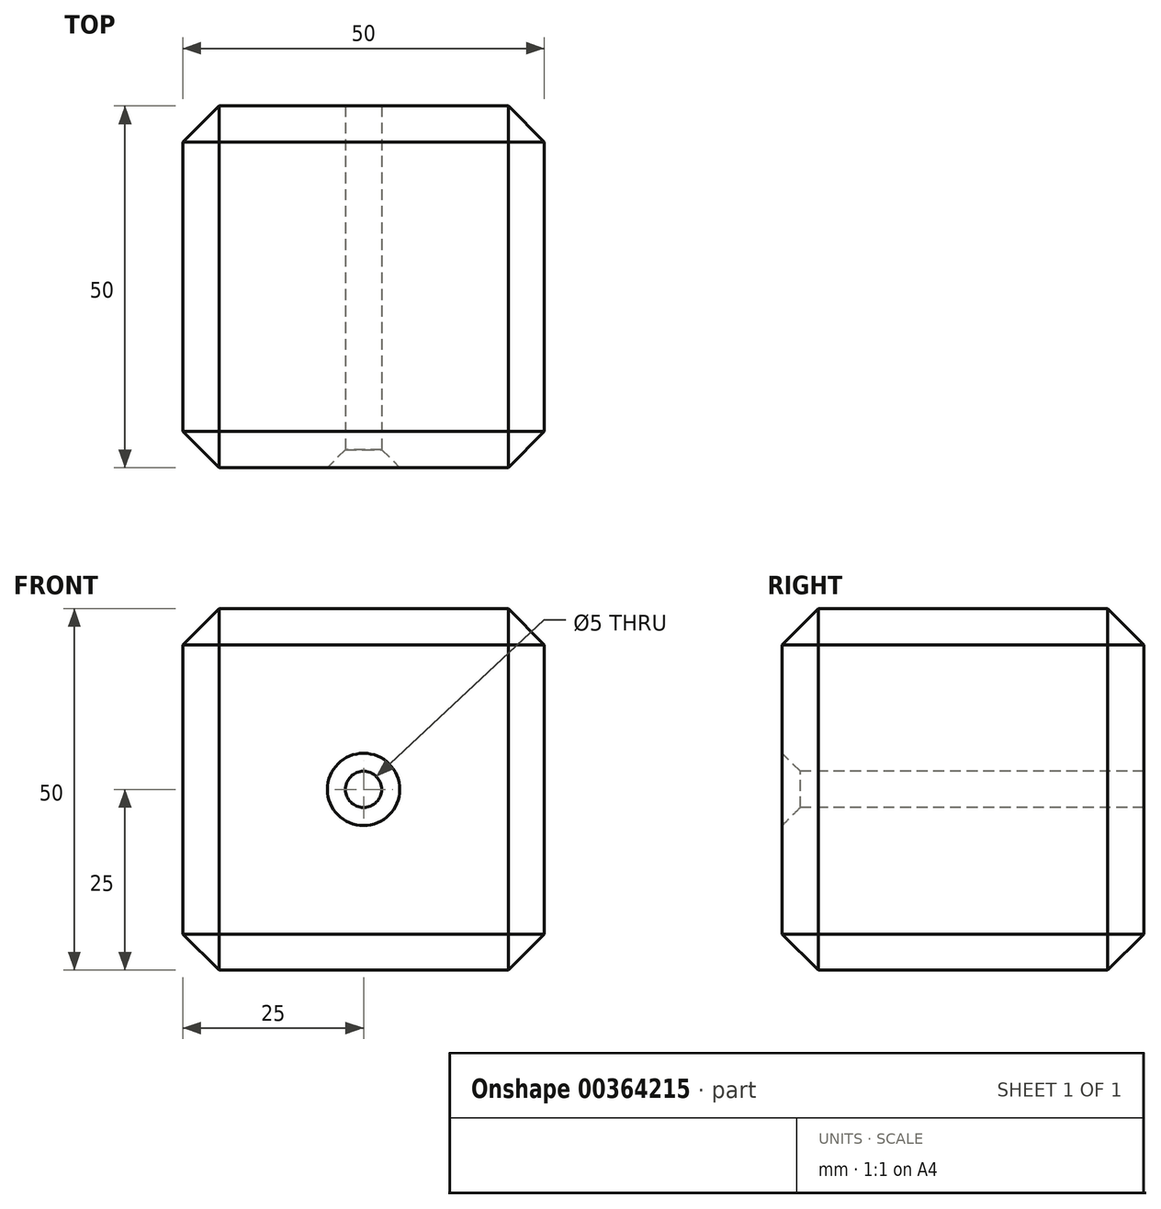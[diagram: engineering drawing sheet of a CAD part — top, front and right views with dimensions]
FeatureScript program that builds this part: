
annotation { "Feature Type Name" : "Feature", "Feature Type Description" : "" }
export const myFeature = defineFeature(function(context is Context, id is Id, definition is map)
    precondition{}
    {
        {
            var Q0;
            Q0=qCreatedBy(makeId("Front.planeOp"),FACE);
            var sketch = newSketch(context, id + "F0", { "sketchPlane" : qUnion([Q0])});
            skLineSegment(sketch, "E0.bottom", {"start": v(25, 25) * mm, "end": v(-25, 25) * mm});
            skLineSegment(sketch, "E0.top", {"start": v(25, -25) * mm, "end": v(-25, -25) * mm});
            skLineSegment(sketch, "E0.left", {"start": v(25, 25) * mm, "end": v(25, -25) * mm});
            skLineSegment(sketch, "E0.right", {"start": v(-25, 25) * mm, "end": v(-25, -25) * mm});
            skPoint(sketch, "E0.middle", {"position": v(0, 0) * mm});
            skSolve(sketch);
        }
        {
            var Q0;
            Q0 = qSketchRegion(id + "F0", true);
            extrude(context, id + "F1", {"entities" : qUnion([Q0]), "depth" : 50 * mm});
        }
        {
            var Q0;
            Q0=makeQuery(id+"F1.opExtrude","SWEPT_EDGE",EDGE,{"disambiguationData":[OSD([sQuery(id+"F0.wireOp",EDGE,"E0.bottom"),sQuery(id+"F0.wireOp",EDGE,"E0.right")])]});
            var Q1;
            Q1=makeQuery(id+"F1.opExtrude","SWEPT_EDGE",EDGE,{"disambiguationData":[OSD([sQuery(id+"F0.wireOp",EDGE,"E0.bottom"),sQuery(id+"F0.wireOp",EDGE,"E0.left")])]});
            var Q2;
            Q2=makeQuery(id+"F1.opExtrude","CAP_EDGE",EDGE,{"disambiguationData":[OSD([sQuery(id+"F0.wireOp",EDGE,"E0.bottom")])],"isStart":false});
            var Q3;
            Q3=makeQuery(id+"F1.opExtrude","CAP_EDGE",EDGE,{"disambiguationData":[OSD([sQuery(id+"F0.wireOp",EDGE,"E0.bottom")])],"isStart":true});
            var Q4;
            Q4=makeQuery(id+"F1.opExtrude","CAP_EDGE",EDGE,{"disambiguationData":[OSD([sQuery(id+"F0.wireOp",EDGE,"E0.right")])],"isStart":false});
            var Q5;
            Q5=makeQuery(id+"F1.opExtrude","CAP_EDGE",EDGE,{"disambiguationData":[OSD([sQuery(id+"F0.wireOp",EDGE,"E0.left")])],"isStart":false});
            var Q6;
            Q6=makeQuery(id+"F1.opExtrude","CAP_EDGE",EDGE,{"disambiguationData":[OSD([sQuery(id+"F0.wireOp",EDGE,"E0.top")])],"isStart":false});
            var Q7;
            Q7=makeQuery(id+"F1.opExtrude","SWEPT_EDGE",EDGE,{"disambiguationData":[OSD([sQuery(id+"F0.wireOp",EDGE,"E0.top"),sQuery(id+"F0.wireOp",EDGE,"E0.right")])]});
            var Q8;
            Q8=makeQuery(id+"F1.opExtrude","CAP_EDGE",EDGE,{"disambiguationData":[OSD([sQuery(id+"F0.wireOp",EDGE,"E0.right")])],"isStart":true});
            var Q9;
            Q9=makeQuery(id+"F1.opExtrude","CAP_EDGE",EDGE,{"disambiguationData":[OSD([sQuery(id+"F0.wireOp",EDGE,"E0.top")])],"isStart":true});
            var Q10;
            Q10=makeQuery(id+"F1.opExtrude","CAP_EDGE",EDGE,{"disambiguationData":[OSD([sQuery(id+"F0.wireOp",EDGE,"E0.left")])],"isStart":true});
            var Q11;
            Q11=makeQuery(id+"F1.opExtrude","SWEPT_EDGE",EDGE,{"disambiguationData":[OSD([sQuery(id+"F0.wireOp",EDGE,"E0.top"),sQuery(id+"F0.wireOp",EDGE,"E0.left")])]});
            chamfer(context, id + "F2", {"entities" : qUnion([Q0, Q1, Q2, Q3, Q4, Q5, Q6, Q7, Q8, Q9, Q10, Q11]), "width" : 5 * mm, "tangentPropagation" : true});
        }
        {
            var Q0;
            Q0=makeQuery(id+"F1.opExtrude","CAP_FACE",FACE,{"disambiguationData":[OSD([sQuery(id+"F0.wireOp",EDGE,"E0.bottom"),sQuery(id+"F0.wireOp",EDGE,"E0.top"),sQuery(id+"F0.wireOp",EDGE,"E0.left"),sQuery(id+"F0.wireOp",EDGE,"E0.right")])],"isStart":false});
            var sketch = newSketch(context, id + "F3", { "sketchPlane" : qUnion([Q0])});
            skCircle(sketch, "E1", {"center": v(0, 0) * mm, "radius": 2.5 * mm});
            skSolve(sketch);
        }
        {
            var Q0;
            Q0=sQuery(id+"F3.wireOp",VERTEX,"E1.center");
            var Q1;
            Q1=makeQuery(id+"F1.opExtrude","SWEPT_BODY",BODY,{"disambiguationData":[OSD([sQuery(id+"F0.wireOp",EDGE,"E0.bottom"),sQuery(id+"F0.wireOp",EDGE,"E0.top"),sQuery(id+"F0.wireOp",EDGE,"E0.left"),sQuery(id+"F0.wireOp",EDGE,"E0.right")])]});
            hole(context, id + "F4", {"style" : HoleStyle.C_SINK, "endStyle" : HoleEndStyle.THROUGH, "holeDiameter" : 5 * mm, "cSinkDiameter" : 10 * mm, "cSinkAngle" : 90 * degree, "isTappedThrough" : true, "tappedDepth" : 12 * mm, "tapClearance" : 3, "locations" : qUnion([Q0]), "scope" : qUnion([Q1])});
        }
    });
